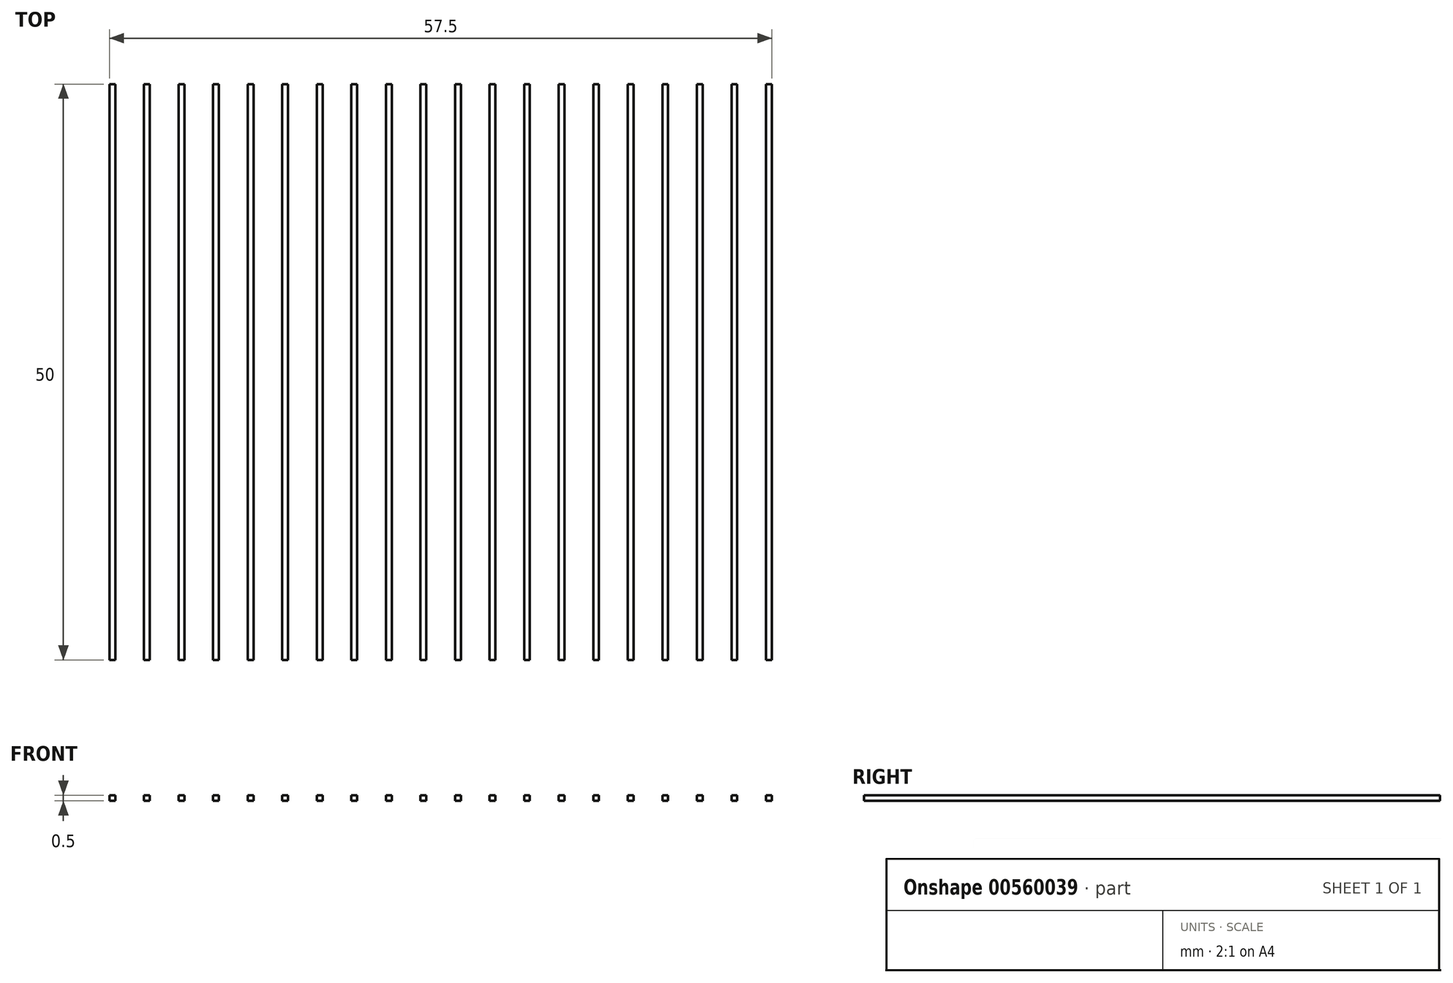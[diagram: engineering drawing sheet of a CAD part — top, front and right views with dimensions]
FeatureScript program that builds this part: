
annotation { "Feature Type Name" : "Feature", "Feature Type Description" : "" }
export const myFeature = defineFeature(function(context is Context, id is Id, definition is map)
    precondition{}
    {
        {
            var Q0;
            Q0=qCreatedBy(makeId("Top.planeOp"),FACE);
            var sketch = newSketch(context, id + "F0", { "sketchPlane" : qUnion([Q0])});
            skLineSegment(sketch, "E0.bottom", {"start": v(-27.05, 25) * mm, "end": v(-27.55, 25) * mm});
            skLineSegment(sketch, "E0.top", {"start": v(-27.05, -25) * mm, "end": v(-27.55, -25) * mm});
            skLineSegment(sketch, "E0.left", {"start": v(-27.05, 25) * mm, "end": v(-27.05, -25) * mm});
            skLineSegment(sketch, "E0.right", {"start": v(-27.55, 25) * mm, "end": v(-27.55, -25) * mm});
            skPoint(sketch, "E0.middle", {"position": v(-27.3, 0) * mm});
            skLineSegment(sketch, "E1.1.0.0", {"start": v(-24.55, 25) * mm, "end": v(-24.55, -25) * mm});
            skLineSegment(sketch, "E1.1.0.1", {"start": v(-24.05, 25) * mm, "end": v(-24.05, -25) * mm});
            skPoint(sketch, "E1.1.0.2", {"position": v(-24.3, 0) * mm});
            skLineSegment(sketch, "E1.1.0.3", {"start": v(-24.05, -25) * mm, "end": v(-24.55, -25) * mm});
            skLineSegment(sketch, "E1.1.0.4", {"start": v(-24.05, 25) * mm, "end": v(-24.55, 25) * mm});
            skLineSegment(sketch, "E1.2.0.0", {"start": v(-21.55, 25) * mm, "end": v(-21.55, -25) * mm});
            skLineSegment(sketch, "E1.2.0.1", {"start": v(-21.05, 25) * mm, "end": v(-21.05, -25) * mm});
            skPoint(sketch, "E1.2.0.2", {"position": v(-21.3, 0) * mm});
            skLineSegment(sketch, "E1.2.0.3", {"start": v(-21.05, -25) * mm, "end": v(-21.55, -25) * mm});
            skLineSegment(sketch, "E1.2.0.4", {"start": v(-21.05, 25) * mm, "end": v(-21.55, 25) * mm});
            skLineSegment(sketch, "E1.3.0.0", {"start": v(-18.55, 25) * mm, "end": v(-18.55, -25) * mm});
            skLineSegment(sketch, "E1.3.0.1", {"start": v(-18.05, 25) * mm, "end": v(-18.05, -25) * mm});
            skPoint(sketch, "E1.3.0.2", {"position": v(-18.3, 0) * mm});
            skLineSegment(sketch, "E1.3.0.3", {"start": v(-18.05, -25) * mm, "end": v(-18.55, -25) * mm});
            skLineSegment(sketch, "E1.3.0.4", {"start": v(-18.05, 25) * mm, "end": v(-18.55, 25) * mm});
            skLineSegment(sketch, "E1.4.0.0", {"start": v(-15.55, 25) * mm, "end": v(-15.55, -25) * mm});
            skLineSegment(sketch, "E1.4.0.1", {"start": v(-15.05, 25) * mm, "end": v(-15.05, -25) * mm});
            skPoint(sketch, "E1.4.0.2", {"position": v(-15.3, 0) * mm});
            skLineSegment(sketch, "E1.4.0.3", {"start": v(-15.05, -25) * mm, "end": v(-15.55, -25) * mm});
            skLineSegment(sketch, "E1.4.0.4", {"start": v(-15.05, 25) * mm, "end": v(-15.55, 25) * mm});
            skLineSegment(sketch, "E1.5.0.0", {"start": v(-12.55, 25) * mm, "end": v(-12.55, -25) * mm});
            skLineSegment(sketch, "E1.5.0.1", {"start": v(-12.05, 25) * mm, "end": v(-12.05, -25) * mm});
            skPoint(sketch, "E1.5.0.2", {"position": v(-12.3, 0) * mm});
            skLineSegment(sketch, "E1.5.0.3", {"start": v(-12.05, -25) * mm, "end": v(-12.55, -25) * mm});
            skLineSegment(sketch, "E1.5.0.4", {"start": v(-12.05, 25) * mm, "end": v(-12.55, 25) * mm});
            skLineSegment(sketch, "E1.6.0.0", {"start": v(-9.55, 25) * mm, "end": v(-9.55, -25) * mm});
            skLineSegment(sketch, "E1.6.0.1", {"start": v(-9.05, 25) * mm, "end": v(-9.05, -25) * mm});
            skPoint(sketch, "E1.6.0.2", {"position": v(-9.3, 0) * mm});
            skLineSegment(sketch, "E1.6.0.3", {"start": v(-9.05, -25) * mm, "end": v(-9.55, -25) * mm});
            skLineSegment(sketch, "E1.6.0.4", {"start": v(-9.05, 25) * mm, "end": v(-9.55, 25) * mm});
            skLineSegment(sketch, "E1.7.0.0", {"start": v(-6.55, 25) * mm, "end": v(-6.55, -25) * mm});
            skLineSegment(sketch, "E1.7.0.1", {"start": v(-6.05, 25) * mm, "end": v(-6.05, -25) * mm});
            skPoint(sketch, "E1.7.0.2", {"position": v(-6.3, 0) * mm});
            skLineSegment(sketch, "E1.7.0.3", {"start": v(-6.05, -25) * mm, "end": v(-6.55, -25) * mm});
            skLineSegment(sketch, "E1.7.0.4", {"start": v(-6.05, 25) * mm, "end": v(-6.55, 25) * mm});
            skLineSegment(sketch, "E1.8.0.0", {"start": v(-3.55, 25) * mm, "end": v(-3.55, -25) * mm});
            skLineSegment(sketch, "E1.8.0.1", {"start": v(-3.05, 25) * mm, "end": v(-3.05, -25) * mm});
            skPoint(sketch, "E1.8.0.2", {"position": v(-3.3, 0) * mm});
            skLineSegment(sketch, "E1.8.0.3", {"start": v(-3.05, -25) * mm, "end": v(-3.55, -25) * mm});
            skLineSegment(sketch, "E1.8.0.4", {"start": v(-3.05, 25) * mm, "end": v(-3.55, 25) * mm});
            skLineSegment(sketch, "E1.9.0.0", {"start": v(-0.55, 25) * mm, "end": v(-0.55, -25) * mm});
            skLineSegment(sketch, "E1.9.0.1", {"start": v(-0.05, 25) * mm, "end": v(-0.05, -25) * mm});
            skPoint(sketch, "E1.9.0.2", {"position": v(-0.3, 0) * mm});
            skLineSegment(sketch, "E1.9.0.3", {"start": v(-0.05, -25) * mm, "end": v(-0.55, -25) * mm});
            skLineSegment(sketch, "E1.9.0.4", {"start": v(-0.05, 25) * mm, "end": v(-0.55, 25) * mm});
            skLineSegment(sketch, "E1.10.0.0", {"start": v(2.45, 25) * mm, "end": v(2.45, -25) * mm});
            skLineSegment(sketch, "E1.10.0.1", {"start": v(2.95, 25) * mm, "end": v(2.95, -25) * mm});
            skPoint(sketch, "E1.10.0.2", {"position": v(2.7, 0) * mm});
            skLineSegment(sketch, "E1.10.0.3", {"start": v(2.95, -25) * mm, "end": v(2.45, -25) * mm});
            skLineSegment(sketch, "E1.10.0.4", {"start": v(2.95, 25) * mm, "end": v(2.45, 25) * mm});
            skLineSegment(sketch, "E1.11.0.0", {"start": v(5.45, 25) * mm, "end": v(5.45, -25) * mm});
            skLineSegment(sketch, "E1.11.0.1", {"start": v(5.95, 25) * mm, "end": v(5.95, -25) * mm});
            skPoint(sketch, "E1.11.0.2", {"position": v(5.7, 0) * mm});
            skLineSegment(sketch, "E1.11.0.3", {"start": v(5.95, -25) * mm, "end": v(5.45, -25) * mm});
            skLineSegment(sketch, "E1.11.0.4", {"start": v(5.95, 25) * mm, "end": v(5.45, 25) * mm});
            skLineSegment(sketch, "E1.12.0.0", {"start": v(8.45, 25) * mm, "end": v(8.45, -25) * mm});
            skLineSegment(sketch, "E1.12.0.1", {"start": v(8.95, 25) * mm, "end": v(8.95, -25) * mm});
            skPoint(sketch, "E1.12.0.2", {"position": v(8.7, 0) * mm});
            skLineSegment(sketch, "E1.12.0.3", {"start": v(8.95, -25) * mm, "end": v(8.45, -25) * mm});
            skLineSegment(sketch, "E1.12.0.4", {"start": v(8.95, 25) * mm, "end": v(8.45, 25) * mm});
            skLineSegment(sketch, "E1.13.0.0", {"start": v(11.45, 25) * mm, "end": v(11.45, -25) * mm});
            skLineSegment(sketch, "E1.13.0.1", {"start": v(11.95, 25) * mm, "end": v(11.95, -25) * mm});
            skPoint(sketch, "E1.13.0.2", {"position": v(11.7, 0) * mm});
            skLineSegment(sketch, "E1.13.0.3", {"start": v(11.95, -25) * mm, "end": v(11.45, -25) * mm});
            skLineSegment(sketch, "E1.13.0.4", {"start": v(11.95, 25) * mm, "end": v(11.45, 25) * mm});
            skLineSegment(sketch, "E1.14.0.0", {"start": v(14.45, 25) * mm, "end": v(14.45, -25) * mm});
            skLineSegment(sketch, "E1.14.0.1", {"start": v(14.95, 25) * mm, "end": v(14.95, -25) * mm});
            skPoint(sketch, "E1.14.0.2", {"position": v(14.7, 0) * mm});
            skLineSegment(sketch, "E1.14.0.3", {"start": v(14.95, -25) * mm, "end": v(14.45, -25) * mm});
            skLineSegment(sketch, "E1.14.0.4", {"start": v(14.95, 25) * mm, "end": v(14.45, 25) * mm});
            skLineSegment(sketch, "E1.15.0.0", {"start": v(17.45, 25) * mm, "end": v(17.45, -25) * mm});
            skLineSegment(sketch, "E1.15.0.1", {"start": v(17.95, 25) * mm, "end": v(17.95, -25) * mm});
            skPoint(sketch, "E1.15.0.2", {"position": v(17.7, 0) * mm});
            skLineSegment(sketch, "E1.15.0.3", {"start": v(17.95, -25) * mm, "end": v(17.45, -25) * mm});
            skLineSegment(sketch, "E1.15.0.4", {"start": v(17.95, 25) * mm, "end": v(17.45, 25) * mm});
            skLineSegment(sketch, "E1.16.0.0", {"start": v(20.45, 25) * mm, "end": v(20.45, -25) * mm});
            skLineSegment(sketch, "E1.16.0.1", {"start": v(20.95, 25) * mm, "end": v(20.95, -25) * mm});
            skPoint(sketch, "E1.16.0.2", {"position": v(20.7, 0) * mm});
            skLineSegment(sketch, "E1.16.0.3", {"start": v(20.95, -25) * mm, "end": v(20.45, -25) * mm});
            skLineSegment(sketch, "E1.16.0.4", {"start": v(20.95, 25) * mm, "end": v(20.45, 25) * mm});
            skLineSegment(sketch, "E1.17.0.0", {"start": v(23.45, 25) * mm, "end": v(23.45, -25) * mm});
            skLineSegment(sketch, "E1.17.0.1", {"start": v(23.95, 25) * mm, "end": v(23.95, -25) * mm});
            skPoint(sketch, "E1.17.0.2", {"position": v(23.7, 0) * mm});
            skLineSegment(sketch, "E1.17.0.3", {"start": v(23.95, -25) * mm, "end": v(23.45, -25) * mm});
            skLineSegment(sketch, "E1.17.0.4", {"start": v(23.95, 25) * mm, "end": v(23.45, 25) * mm});
            skLineSegment(sketch, "E1.18.0.0", {"start": v(26.45, 25) * mm, "end": v(26.45, -25) * mm});
            skLineSegment(sketch, "E1.18.0.1", {"start": v(26.95, 25) * mm, "end": v(26.95, -25) * mm});
            skPoint(sketch, "E1.18.0.2", {"position": v(26.7, 0) * mm});
            skLineSegment(sketch, "E1.18.0.3", {"start": v(26.95, -25) * mm, "end": v(26.45, -25) * mm});
            skLineSegment(sketch, "E1.18.0.4", {"start": v(26.95, 25) * mm, "end": v(26.45, 25) * mm});
            skLineSegment(sketch, "E1.19.0.0", {"start": v(29.45, 25) * mm, "end": v(29.45, -25) * mm});
            skLineSegment(sketch, "E1.19.0.1", {"start": v(29.95, 25) * mm, "end": v(29.95, -25) * mm});
            skPoint(sketch, "E1.19.0.2", {"position": v(29.7, 0) * mm});
            skLineSegment(sketch, "E1.19.0.3", {"start": v(29.95, -25) * mm, "end": v(29.45, -25) * mm});
            skLineSegment(sketch, "E1.19.0.4", {"start": v(29.95, 25) * mm, "end": v(29.45, 25) * mm});
            skLineSegment(sketch, "E1.direction1", {"start": v(-27.55, -25) * mm, "end": v(-24.55, -25) * mm, "construction": true});
            skSolve(sketch);
        }
        {
            var Q0;
            Q0 = qSketchRegion(id + "F0", true);
            extrude(context, id + "F1", {"entities" : qUnion([Q0]), "depth" : 0.5 * mm, "offsetDistance" : 25 * mm});
        }
    });
